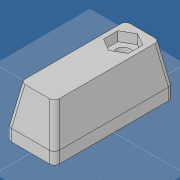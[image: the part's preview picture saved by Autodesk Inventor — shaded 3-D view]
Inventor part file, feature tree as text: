
AUTODESK INVENTOR PART (.ipt)
format: ipt  version: 2019 (Build 230136000, 136)  size: 151,552 bytes
history: native  units: mm
features: extrude x5, sketch x3, other x2, fillet x1
ambient origin geometry x8: Origin, YZ Plane, XZ Plane, XY Plane, X Axis, Y Axis, Z Axis, Center Point
bodies: Volumenkörper1 (feature_tree)
feature tree (11):
  sketch  "Skizze1"  dims[d0=10.5mm d1=20.0mm]
  extrude  "Extrusion1"  Depth=20.0mm
  extrude  "Extrusion2"  Depth=50.0mm
  extrude  "Extrusion3"  Depth=6.0mm
  extrude  "Extrusion4"  Depth=4.0mm TaperAngle=0.0deg
  extrude  "Extrusion5"  Depth=17.0mm TaperAngle=0.0deg
  fillet  "Rundung1"  Radius=5.0mm
  sketch  "Skizze2"  dims[d2=50.0mm d3=5.0mm]
  sketch  "Skizze3"  dims[d4=2.0mm d5=0.0mm d6=6.0mm d8=4.0mm d9=0.0mm d10=17.0mm d11=0.0mm d12=5.0mm d13=1.745329mm d14=1.745329mm d15=14.0mm d16=0.0mm d17=1.745329mm d18=1.745329mm d19=5.0mm d20=14.0mm d21=0.0mm d22=2.0mm]
  other  "Schnittkanten projizieren1"
  other  "Schnittkanten projizieren2"
